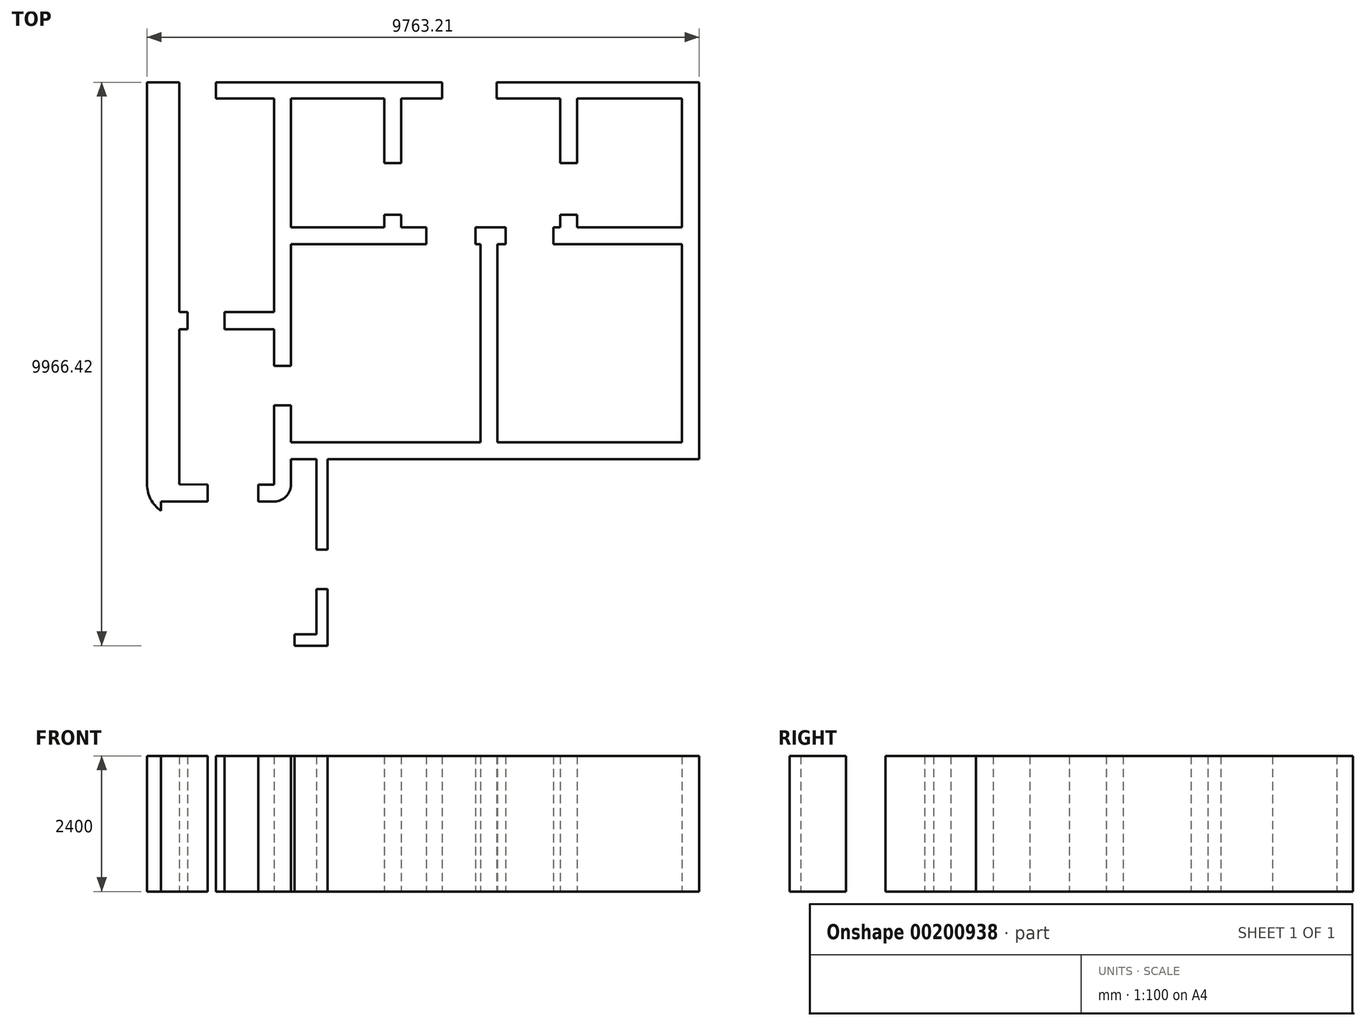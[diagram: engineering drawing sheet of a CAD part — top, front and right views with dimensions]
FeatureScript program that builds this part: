
annotation { "Feature Type Name" : "Feature", "Feature Type Description" : "" }
export const myFeature = defineFeature(function(context is Context, id is Id, definition is map)
    precondition{}
    {
        {
            var Q0;
            Q0=qCreatedBy(makeId("Top.planeOp"),FACE);
            var sketch = newSketch(context, id + "F0", { "sketchPlane" : qUnion([Q0])});
            skLineSegment(sketch, "E0", {"start": v(0, 0) * mm, "end": v(0, 2683.78) * mm});
            skLineSegment(sketch, "E1", {"start": v(0, 0) * mm, "end": v(4232.43, 0) * mm});
            skLineSegment(sketch, "E2", {"start": v(300, 2667.57) * mm, "end": v(300, 300) * mm});
            skLineSegment(sketch, "E3", {"start": v(300, 300) * mm, "end": v(3650, 300) * mm});
            skLineSegment(sketch, "E4", {"start": v(300, 300) * mm, "end": v(300, 950) * mm});
            skLineSegment(sketch, "E5", {"start": v(300, 950) * mm, "end": v(0, 950) * mm});
            skLineSegment(sketch, "E6", {"start": v(0, 950) * mm, "end": v(0, 1650) * mm});
            skLineSegment(sketch, "E7", {"start": v(0, 1650) * mm, "end": v(300, 1650) * mm});
            skLineSegment(sketch, "E8", {"start": v(300, 1650) * mm, "end": v(300, 3800) * mm});
            skLineSegment(sketch, "E9", {"start": v(300, 3800) * mm, "end": v(3650, 3800) * mm});
            skLineSegment(sketch, "E10", {"start": v(0, 6030.04) * mm, "end": v(0, 0) * mm});
            skLineSegment(sketch, "E11", {"start": v(300, 1650) * mm, "end": v(300, 950) * mm});
            skLineSegment(sketch, "E12", {"start": v(-2245.72, 6666.42) * mm, "end": v(-2245.72, -445) * mm});
            skLineSegment(sketch, "E13", {"start": v(0, 0) * mm, "end": v(0, -450) * mm});
            skLineSegment(sketch, "E14", {"start": v(0, -450) * mm, "end": v(-2000, -450) * mm});
            skLineSegment(sketch, "E15", {"start": v(300, 0) * mm, "end": v(300, -450) * mm});
            skLineSegment(sketch, "E16", {"start": v(0, -750) * mm, "end": v(-2000, -750) * mm});
            skLineSegment(sketch, "E17", {"start": v(750, 0) * mm, "end": v(750, -2850) * mm});
            skLineSegment(sketch, "E18", {"start": v(-2000, -750) * mm, "end": v(-2000, -2350) * mm});
            skLineSegment(sketch, "E19", {"start": v(950, 0) * mm, "end": v(950, -3300) * mm});
            skLineSegment(sketch, "E20", {"start": v(0, 2300) * mm, "end": v(-1676, 2300) * mm});
            skLineSegment(sketch, "E21", {"start": v(-2200, -668.6) * mm, "end": v(-2200, -2470.28) * mm});
            skArc(sketch, "E22", {"start": v(-2245.72, -445) * mm, "mid": v(-2078.85, -847.85) * mm, "end": v(-1676, -1014.72) * mm});
            skArc(sketch, "E23", {"start": v(0, -750) * mm, "mid": v(212.13, -662.13) * mm, "end": v(300, -450) * mm});
            skPoint(sketch, "E24.orphan", {"position": v(300, -750) * mm});
            skPoint(sketch, "E25.end.orphan", {"position": v(0, 300) * mm});
            skLineSegment(sketch, "E26", {"start": v(-1676, -445) * mm, "end": v(-1676, 2300) * mm});
            skLineSegment(sketch, "E27.bottom", {"start": v(-1176, -450) * mm, "end": v(-276, -450) * mm});
            skLineSegment(sketch, "E27.top", {"start": v(-1176, -750) * mm, "end": v(-276, -750) * mm});
            skLineSegment(sketch, "E27.left", {"start": v(-1176, -450) * mm, "end": v(-1176, -750) * mm});
            skLineSegment(sketch, "E27.right", {"start": v(-276, -450) * mm, "end": v(-276, -750) * mm});
            skLineSegment(sketch, "E28", {"start": v(-1676, -445) * mm, "end": v(-1176, -450) * mm});
            skArc(sketch, "E29", {"start": v(-596.36, -3117.98) * mm, "mid": v(-591.49, -3109) * mm, "end": v(-586.67, -3100) * mm});
            skLineSegment(sketch, "E30.bottom", {"start": v(750, -2300) * mm, "end": v(950, -2300) * mm});
            skLineSegment(sketch, "E30.top", {"start": v(750, -1600) * mm, "end": v(950, -1600) * mm});
            skLineSegment(sketch, "E30.left", {"start": v(750, -2300) * mm, "end": v(750, -1600) * mm});
            skLineSegment(sketch, "E30.right", {"start": v(950, -2300) * mm, "end": v(950, -1600) * mm});
            skLineSegment(sketch, "E31", {"start": v(750, -3100) * mm, "end": v(-586.67, -3100) * mm});
            skLineSegment(sketch, "E32", {"start": v(750, -3100) * mm, "end": v(750, -2850) * mm});
            skLineSegment(sketch, "E33", {"start": v(-2000, -2350) * mm, "end": v(-586.67, -3100) * mm});
            skPoint(sketch, "E34.orphan", {"position": v(750, -3117.98) * mm});
            skPoint(sketch, "E35.orphan", {"position": v(950, -3100) * mm});
            skLineSegment(sketch, "E36", {"start": v(950, -3300) * mm, "end": v(-636.45, -3300) * mm});
            skLineSegment(sketch, "E37", {"start": v(-2200, -2470.28) * mm, "end": v(-636.45, -3300) * mm});
            skPoint(sketch, "E38.orphan", {"position": v(950, -6600) * mm});
            skLineSegment(sketch, "E39.bottom", {"start": v(-636.45, -3300) * mm, "end": v(363.55, -3300) * mm});
            skLineSegment(sketch, "E39.top", {"start": v(-636.45, -3100) * mm, "end": v(363.55, -3100) * mm});
            skLineSegment(sketch, "E39.left", {"start": v(-636.45, -3300) * mm, "end": v(-636.45, -3100) * mm});
            skLineSegment(sketch, "E39.right", {"start": v(363.55, -3300) * mm, "end": v(363.55, -3100) * mm});
            skPoint(sketch, "E40.orphan", {"position": v(-1676, 3490.07) * mm});
            skLineSegment(sketch, "E41", {"start": v(0, 2600) * mm, "end": v(-1676, 2600) * mm});
            skLineSegment(sketch, "E42", {"start": v(-1676, 2600) * mm, "end": v(-1676, 3995.44) * mm});
            skLineSegment(sketch, "E43.bottom", {"start": v(300, 4100) * mm, "end": v(1948.86, 4100) * mm});
            skLineSegment(sketch, "E43.top", {"start": v(300, 6380.68) * mm, "end": v(1948.86, 6380.68) * mm});
            skLineSegment(sketch, "E43.left", {"start": v(300, 4100) * mm, "end": v(300, 6380.68) * mm});
            skLineSegment(sketch, "E43.right", {"start": v(1948.86, 4100) * mm, "end": v(1948.86, 6380.68) * mm});
            skLineSegment(sketch, "E44.bottom", {"start": v(2248.86, 6380.68) * mm, "end": v(5063.5, 6380.68) * mm});
            skLineSegment(sketch, "E44.top", {"start": v(2248.86, 4100) * mm, "end": v(5063.5, 4100) * mm});
            skLineSegment(sketch, "E44.left", {"start": v(2248.86, 6380.68) * mm, "end": v(2248.86, 4100) * mm});
            skLineSegment(sketch, "E44.right", {"start": v(5063.5, 6380.68) * mm, "end": v(5063.5, 4100) * mm});
            skLineSegment(sketch, "E45.bottom", {"start": v(5363.5, 6380.68) * mm, "end": v(7217.5, 6380.68) * mm});
            skLineSegment(sketch, "E45.top", {"start": v(5363.5, 4100) * mm, "end": v(7217.5, 4100) * mm});
            skLineSegment(sketch, "E45.left", {"start": v(5363.5, 6380.68) * mm, "end": v(5363.5, 4100) * mm});
            skLineSegment(sketch, "E45.right", {"start": v(7217.5, 6380.68) * mm, "end": v(7217.5, 4100) * mm});
            skLineSegment(sketch, "E46.left", {"start": v(300, 3800) * mm, "end": v(300, 300) * mm});
            skLineSegment(sketch, "E46.right", {"start": v(3650, 3800) * mm, "end": v(3650, 300) * mm});
            skLineSegment(sketch, "E47.bottom", {"start": v(3950, 3800) * mm, "end": v(7217.5, 3800) * mm});
            skLineSegment(sketch, "E47.top", {"start": v(3950, 300) * mm, "end": v(7217.5, 300) * mm});
            skLineSegment(sketch, "E47.left", {"start": v(3950, 3800) * mm, "end": v(3950, 300) * mm});
            skLineSegment(sketch, "E47.right", {"start": v(7217.5, 3800) * mm, "end": v(7217.5, 300) * mm});
            skLineSegment(sketch, "E48.bottom", {"start": v(0, 6666.42) * mm, "end": v(7517.5, 6666.42) * mm});
            skLineSegment(sketch, "E48.top", {"start": v(0, 0) * mm, "end": v(7517.5, 0) * mm});
            skLineSegment(sketch, "E48.left", {"start": v(0, 6380.68) * mm, "end": v(0, 0) * mm});
            skLineSegment(sketch, "E48.right", {"start": v(7517.5, 6666.42) * mm, "end": v(7517.5, 0) * mm});
            skLineSegment(sketch, "E49.bottom", {"start": v(950, -3100) * mm, "end": v(7317.5, -3100) * mm});
            skLineSegment(sketch, "E49.top", {"start": v(950, -3300) * mm, "end": v(7517.5, -3300) * mm});
            skLineSegment(sketch, "E49.left", {"start": v(950, -3100) * mm, "end": v(950, -3300) * mm});
            skLineSegment(sketch, "E50.bottom", {"start": v(7517.5, 0) * mm, "end": v(7317.5, 0) * mm});
            skLineSegment(sketch, "E50.top", {"start": v(7517.5, -3300) * mm, "end": v(7317.5, -3300) * mm});
            skLineSegment(sketch, "E50.left", {"start": v(7517.5, 0) * mm, "end": v(7517.5, -3300) * mm});
            skLineSegment(sketch, "E50.right", {"start": v(7317.5, 0) * mm, "end": v(7317.5, -3100) * mm});
            skPoint(sketch, "E49.right.end.orphan", {"position": v(7755.82, -3300) * mm});
            skLineSegment(sketch, "E51.bottom", {"start": v(-1676, 2600) * mm, "end": v(0, 2600) * mm});
            skLineSegment(sketch, "E51.top", {"start": v(-1676, 6380.68) * mm, "end": v(0, 6380.68) * mm});
            skLineSegment(sketch, "E51.left", {"start": v(-1676, 2600) * mm, "end": v(-1676, 6380.68) * mm});
            skLineSegment(sketch, "E51.right", {"start": v(0, 2600) * mm, "end": v(0, 6380.68) * mm});
            skLineSegment(sketch, "E52.bottom", {"start": v(0, 4100) * mm, "end": v(-1341.66, 4100) * mm});
            skLineSegment(sketch, "E52.top", {"start": v(0, 6380.68) * mm, "end": v(-1341.66, 6380.68) * mm});
            skLineSegment(sketch, "E52.left", {"start": v(0, 4100) * mm, "end": v(0, 6380.68) * mm});
            skLineSegment(sketch, "E52.right", {"start": v(-1341.66, 4100) * mm, "end": v(-1341.66, 6380.68) * mm});
            skLineSegment(sketch, "E53", {"start": v(0, 6666.42) * mm, "end": v(-2245.72, 6666.42) * mm});
            skLineSegment(sketch, "E54.bottom", {"start": v(-1676, 6380.68) * mm, "end": v(-1026, 6380.68) * mm});
            skLineSegment(sketch, "E54.top", {"start": v(-1676, 6666.42) * mm, "end": v(-1026, 6666.42) * mm});
            skLineSegment(sketch, "E54.left", {"start": v(-1676, 6380.68) * mm, "end": v(-1676, 6666.42) * mm});
            skLineSegment(sketch, "E54.right", {"start": v(-1026, 6380.68) * mm, "end": v(-1026, 6666.42) * mm});
            skLineSegment(sketch, "E55.bottom", {"start": v(-1526, 2300) * mm, "end": v(-876, 2300) * mm});
            skLineSegment(sketch, "E55.top", {"start": v(-1526, 2600) * mm, "end": v(-876, 2600) * mm});
            skLineSegment(sketch, "E55.left", {"start": v(-1526, 2300) * mm, "end": v(-1526, 2600) * mm});
            skLineSegment(sketch, "E55.right", {"start": v(-876, 2300) * mm, "end": v(-876, 2600) * mm});
            skLineSegment(sketch, "E56.bottom", {"start": v(2973.97, 6666.42) * mm, "end": v(3935.1, 6666.42) * mm});
            skLineSegment(sketch, "E56.top", {"start": v(2973.97, 6380.68) * mm, "end": v(3935.1, 6380.68) * mm});
            skLineSegment(sketch, "E56.left", {"start": v(2973.97, 6666.42) * mm, "end": v(2973.97, 6380.68) * mm});
            skLineSegment(sketch, "E56.right", {"start": v(3935.1, 6666.42) * mm, "end": v(3935.1, 6380.68) * mm});
            skLineSegment(sketch, "E57.bottom", {"start": v(1948.86, 4325.75) * mm, "end": v(2248.86, 4325.75) * mm});
            skLineSegment(sketch, "E57.top", {"start": v(1948.86, 5240.34) * mm, "end": v(2248.86, 5240.34) * mm});
            skLineSegment(sketch, "E57.left", {"start": v(1948.86, 4325.75) * mm, "end": v(1948.86, 5240.34) * mm});
            skLineSegment(sketch, "E57.right", {"start": v(2248.86, 4325.75) * mm, "end": v(2248.86, 5240.34) * mm});
            skLineSegment(sketch, "E58.bottom", {"start": v(5063.5, 4325.75) * mm, "end": v(5363.5, 4325.75) * mm});
            skLineSegment(sketch, "E58.top", {"start": v(5063.5, 5240.34) * mm, "end": v(5363.5, 5240.34) * mm});
            skLineSegment(sketch, "E58.left", {"start": v(5063.5, 4325.75) * mm, "end": v(5063.5, 5240.34) * mm});
            skLineSegment(sketch, "E58.right", {"start": v(5363.5, 4325.75) * mm, "end": v(5363.5, 5240.34) * mm});
            skLineSegment(sketch, "E59.bottom", {"start": v(4099.61, 3800) * mm, "end": v(4938.76, 3800) * mm});
            skLineSegment(sketch, "E59.top", {"start": v(4099.61, 4100) * mm, "end": v(4938.76, 4100) * mm});
            skLineSegment(sketch, "E59.left", {"start": v(4099.61, 3800) * mm, "end": v(4099.61, 4100) * mm});
            skLineSegment(sketch, "E59.right", {"start": v(4938.76, 3800) * mm, "end": v(4938.76, 4100) * mm});
            skLineSegment(sketch, "E60.bottom", {"start": v(3566.64, 3800) * mm, "end": v(2693.47, 3800) * mm});
            skLineSegment(sketch, "E60.top", {"start": v(3566.64, 4100) * mm, "end": v(2693.47, 4100) * mm});
            skLineSegment(sketch, "E60.left", {"start": v(3566.64, 3800) * mm, "end": v(3566.64, 4100) * mm});
            skLineSegment(sketch, "E60.right", {"start": v(2693.47, 3800) * mm, "end": v(2693.47, 4100) * mm});
            skSolve(sketch);
        }
        {
            var Q0;
            {var subQ5=sQuery(id+"F0.wireOp",EDGE,"E12");Q0=makeQuery(id+"F0.imprint","IMPRINT",FACE,{"disambiguationData":[TD([[makeQuery(id+"F0.imprint","IMPRINT",EDGE,{"derivedFrom":subQ5}),1.0]])]});}
            var Q1;
            {var subQ2=sQuery(id+"F0.wireOp",EDGE,"E30.bottom");Q1=makeQuery(id+"F0.imprint","IMPRINT",FACE,{"disambiguationData":[TD([[makeQuery(id+"F0.imprint","IMPRINT",EDGE,{"derivedFrom":subQ2}),-1.0]])]});}
            var Q2;
            {var subQ3=sQuery(id+"F0.wireOp",EDGE,"E30.top");Q2=makeQuery(id+"F0.imprint","IMPRINT",FACE,{"disambiguationData":[TD([[makeQuery(id+"F0.imprint","IMPRINT",EDGE,{"derivedFrom":subQ3}),1.0]])]});}
            var Q3;
            {var subQ5=sQuery(id+"F0.wireOp",EDGE,"E5");Q3=makeQuery(id+"F0.imprint","IMPRINT",FACE,{"disambiguationData":[TD([[makeQuery(id+"F0.imprint","IMPRINT",EDGE,{"derivedFrom":subQ5}),1.0]])]});}
            var Q4;
            {var subQ16=sQuery(id+"F0.wireOp",EDGE,"E7");Q4=makeQuery(id+"F0.imprint","IMPRINT",FACE,{"disambiguationData":[TD([[makeQuery(id+"F0.imprint","IMPRINT",EDGE,{"derivedFrom":subQ16}),1.0]])]});}
            var Q5;
            {var subQ3=sQuery(id+"F0.wireOp",EDGE,"E55.right");Q5=makeQuery(id+"F0.imprint","IMPRINT",FACE,{"disambiguationData":[TD([[makeQuery(id+"F0.imprint","IMPRINT",EDGE,{"derivedFrom":subQ3}),-1.0]])]});}
            var Q6;
            {var subQ5=sQuery(id+"F0.wireOp",EDGE,"E13");Q6=makeQuery(id+"F0.imprint","IMPRINT",FACE,{"disambiguationData":[TD([[makeQuery(id+"F0.imprint","IMPRINT",EDGE,{"derivedFrom":subQ5}),1.0]])]});}
            var Q7;
            {var subQ0=sQuery(id+"F0.wireOp",EDGE,"E59.left");Q7=makeQuery(id+"F0.imprint","IMPRINT",FACE,{"disambiguationData":[TD([[makeQuery(id+"F0.imprint","IMPRINT",EDGE,{"derivedFrom":subQ0}),1.0]])]});}
            extrude(context, id + "F1", {"entities" : qUnion([Q0, Q1, Q2, Q3, Q4, Q5, Q6, Q7]), "depth" : 2400 * mm});
        }
    });
